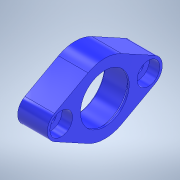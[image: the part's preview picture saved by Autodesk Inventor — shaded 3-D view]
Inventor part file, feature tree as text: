
AUTODESK INVENTOR PART (.ipt)
format: ipt  version: 2022 (Build 260153000, 153)  size: 166,400 bytes
history: native  units: in
note: dims shown in document units (in); Inventor stores cm internally (conversion verified against a paired STEP export)
features: other x3, extrude x2, sketch x2, chamfer x1, projected_geometry x1
ambient origin geometry x8: Origin, YZ Plane, XZ Plane, XY Plane, X Axis, Y Axis, Z Axis, Center Point
bodies: Solid1 (feature_tree)
feature tree (9):
  other  "XY Drive Bearing Holder.ipt"
  extrude  "Extrusion1"  Depth=0.1181in TaperAngle=0.0deg
  chamfer  "Chamfer1"  Distance=0.0197in Angle=45.0deg
  extrude  "Extrusion2"  [1 undecoded]
  other  "Solid3::XY Drive Bearing Holder.ipt"
  other  "TaggingFeature1"
  sketch  "Sketch1"  dims[d0=0.3937in d1=0.1181in d2=0.0in d3=0.0197in d4=0.125in d5=45.0deg]
  sketch  "Sketch2"  dims[d6=0.1181in d7=0.0in]
  projected_geometry  "Projected Loop1"
note: 1 required parameter value undecoded (feature->parameter linkage not recoverable at this tier; creation-order binding heuristic only, values carry confidence <= 0.55)
